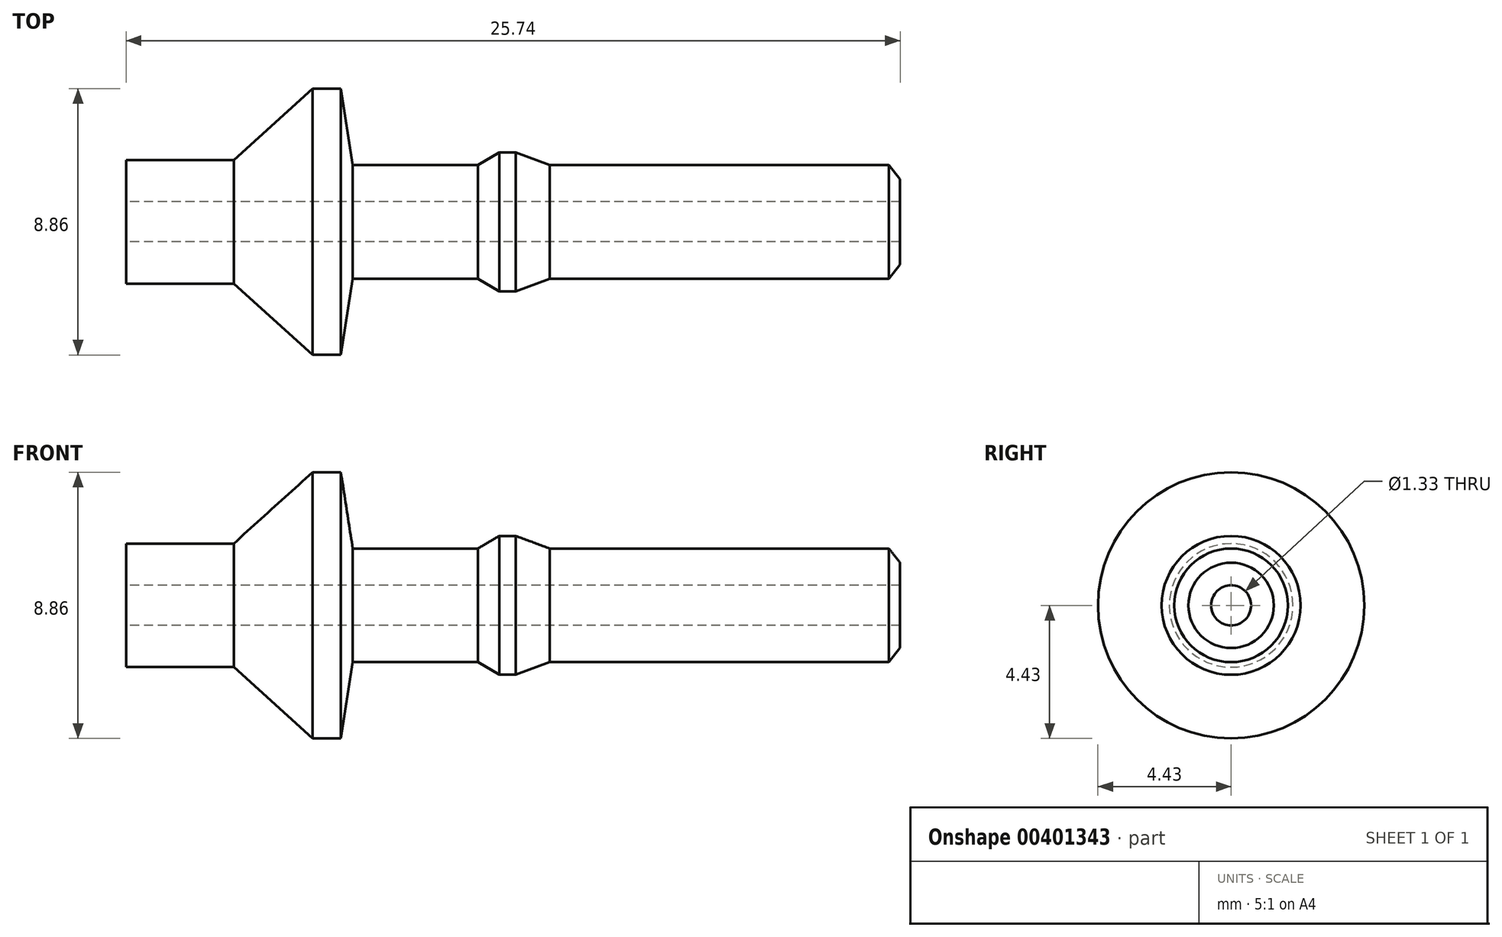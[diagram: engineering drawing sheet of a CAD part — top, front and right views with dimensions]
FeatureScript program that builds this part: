
annotation { "Feature Type Name" : "Feature", "Feature Type Description" : "" }
export const myFeature = defineFeature(function(context is Context, id is Id, definition is map)
    precondition{}
    {
        {
            var Q0;
            Q0=qCreatedBy(makeId("Front.planeOp"),FACE);
            var sketch = newSketch(context, id + "F0", { "sketchPlane" : qUnion([Q0])});
            skLineSegment(sketch, "E0", {"start": v(-5.12, 0.67) * mm, "end": v(20.62, 0.67) * mm});
            skLineSegment(sketch, "E1", {"start": v(20.62, 0.67) * mm, "end": v(20.62, 1.42) * mm});
            skLineSegment(sketch, "E2", {"start": v(20.62, 1.42) * mm, "end": v(20.25, 1.9) * mm});
            skLineSegment(sketch, "E3", {"start": v(20.25, 1.9) * mm, "end": v(8.97, 1.9) * mm});
            skLineSegment(sketch, "E4", {"start": v(8.97, 1.9) * mm, "end": v(7.84, 2.31) * mm});
            skLineSegment(sketch, "E5", {"start": v(7.84, 2.31) * mm, "end": v(7.29, 2.31) * mm});
            skLineSegment(sketch, "E6", {"start": v(7.29, 2.31) * mm, "end": v(6.58, 1.89) * mm});
            skLineSegment(sketch, "E7", {"start": v(6.58, 1.89) * mm, "end": v(2.42, 1.89) * mm});
            skLineSegment(sketch, "E8", {"start": v(2.42, 1.89) * mm, "end": v(2.02, 4.43) * mm});
            skLineSegment(sketch, "E9", {"start": v(-5.12, 2.06) * mm, "end": v(-5.12, 0.67) * mm});
            skLineSegment(sketch, "E10", {"start": v(2.02, 4.43) * mm, "end": v(1.08, 4.43) * mm});
            skLineSegment(sketch, "E11", {"start": v(-6.85, 0) * mm, "end": v(25.14, 0) * mm});
            skLineSegment(sketch, "E12", {"start": v(1.08, 4.43) * mm, "end": v(-1.54, 2.06) * mm});
            skLineSegment(sketch, "E13", {"start": v(-1.54, 2.06) * mm, "end": v(-5.12, 2.06) * mm});
            skSolve(sketch);
        }
        {
            var Q0;
            Q0 = qSketchRegion(id + "F0", true);
            var Q1;
            Q1=sQuery(id+"F0.wireOp",EDGE,"E11");
            revolve(context, id + "F1", {"entities" : qUnion([Q0]), "axis" : qUnion([Q1]), "revolveType" : RevolveType.FULL});
        }
    });
